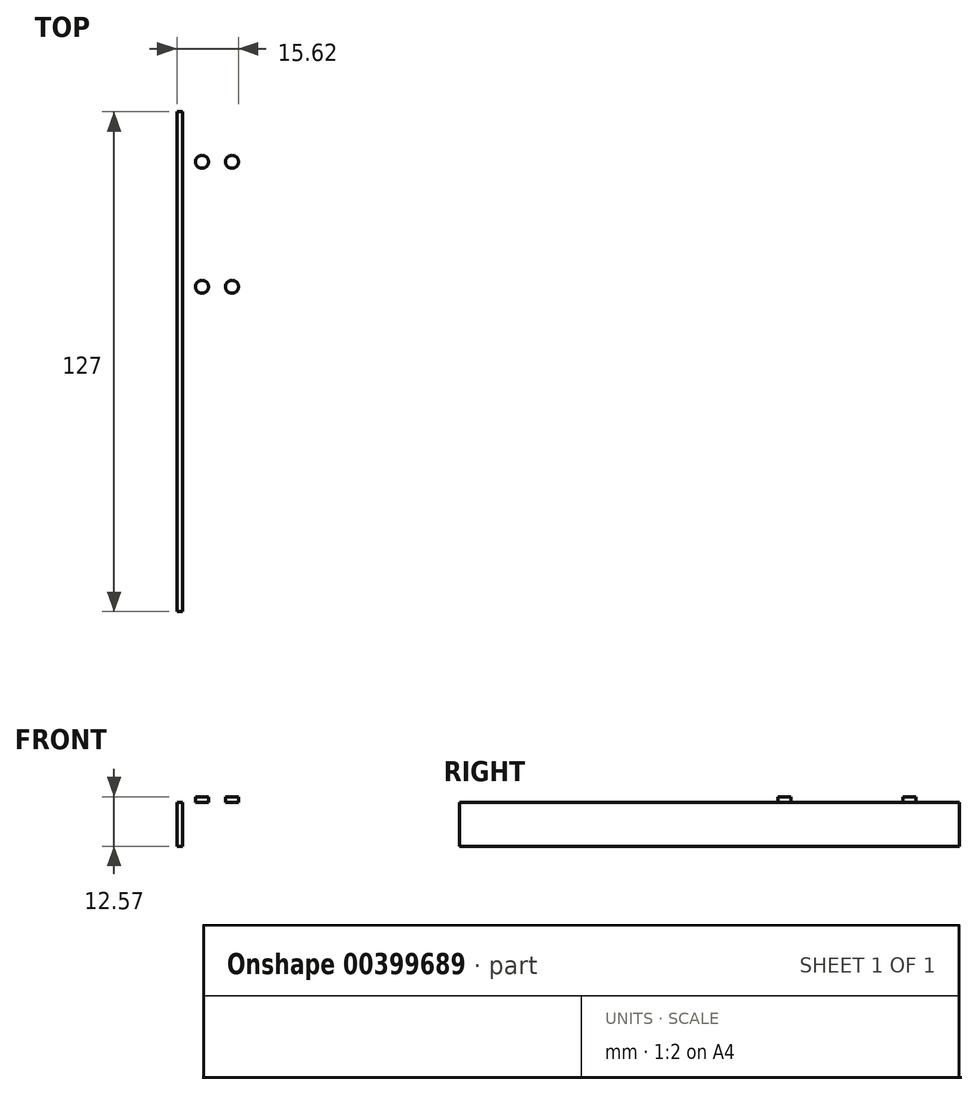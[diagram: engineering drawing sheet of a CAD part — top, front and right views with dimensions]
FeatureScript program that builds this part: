
annotation { "Feature Type Name" : "Feature", "Feature Type Description" : "" }
export const myFeature = defineFeature(function(context is Context, id is Id, definition is map)
    precondition{}
    {
        {
            var Q0;
            Q0=qCreatedBy(makeId("Front.planeOp"),FACE);
            var sketch = newSketch(context, id + "F0", { "sketchPlane" : qUnion([Q0])});
            skLineSegment(sketch, "E0.bottom", {"start": v(0, -11.1) * mm, "end": v(-1.47, -11.1) * mm});
            skLineSegment(sketch, "E0.top", {"start": v(0, 1.47) * mm, "end": v(-1.47, 1.47) * mm});
            skLineSegment(sketch, "E0.left", {"start": v(0, -11.1) * mm, "end": v(0, 1.47) * mm});
            skLineSegment(sketch, "E0.right", {"start": v(-1.47, -11.1) * mm, "end": v(-1.47, 1.47) * mm});
            skLineSegment(sketch, "E1.bottom", {"start": v(-1.47, 1.47) * mm, "end": v(17.58, 1.47) * mm});
            skLineSegment(sketch, "E1.top", {"start": v(-1.47, 0) * mm, "end": v(17.58, 0) * mm});
            skLineSegment(sketch, "E1.left", {"start": v(-1.47, 1.47) * mm, "end": v(-1.47, 0) * mm});
            skLineSegment(sketch, "E1.right", {"start": v(17.58, 1.47) * mm, "end": v(17.58, 0) * mm});
            skSolve(sketch);
        }
        {
            var Q0;
            {var subQ0=sQuery(id+"F0.wireOp",EDGE,"E0.bottom");Q0=makeQuery(id+"F0.imprint","IMPRINT",FACE,{"disambiguationData":[TD([[makeQuery(id+"F0.imprint","IMPRINT",EDGE,{"derivedFrom":subQ0}),-1.0]])]});}
            var Q1;
            {var subQ5=sQuery(id+"F0.wireOp",EDGE,"E1.left");Q1=makeQuery(id+"F0.imprint","IMPRINT",FACE,{"disambiguationData":[TD([[makeQuery(id+"F0.imprint","IMPRINT",EDGE,{"derivedFrom":subQ5}),1.0]])]});}
            var Q2;
            {var subQ5=sQuery(id+"F0.wireOp",EDGE,"E1.right");Q2=makeQuery(id+"F0.imprint","IMPRINT",FACE,{"disambiguationData":[TD([[makeQuery(id+"F0.imprint","IMPRINT",EDGE,{"derivedFrom":subQ5}),-1.0]])]});}
            extrude(context, id + "F1", {"entities" : qUnion([Q0, Q1, Q2]), "endBound" : BoundingType.SYMMETRIC, "depth" : 127 * mm});
        }
        {
            var Q0;
            Q0=makeQuery(id+"F1.opExtrude","SWEPT_FACE",FACE,{"disambiguationData":[OSD([sQuery(id+"F0.wireOp",EDGE,"E1.bottom")])]});
            var sketch = newSketch(context, id + "F2", { "sketchPlane" : qUnion([Q0])});
            skLineSegment(sketch, "E2", {"start": v(-1.47, 0) * mm, "end": v(17.58, 0) * mm, "construction": true});
            skLineSegment(sketch, "E3.0", {"start": v(17.58, -63.5) * mm, "end": v(17.58, 63.5) * mm, "construction": true});
            skLineSegment(sketch, "E4.0", {"start": v(-1.47, -63.5) * mm, "end": v(17.58, -63.5) * mm, "construction": true});
            skLineSegment(sketch, "E5", {"start": v(-1.47, -50.8) * mm, "end": v(17.58, -50.8) * mm, "construction": true});
            skCircle(sketch, "E6", {"center": v(12.5, -50.8) * mm, "radius": 1.65 * mm});
            skCircle(sketch, "E7", {"center": v(4.88, -50.8) * mm, "radius": 1.65 * mm});
            skLineSegment(sketch, "E8", {"start": v(4.88, -49.15) * mm, "end": v(12.5, -49.15) * mm});
            skLineSegment(sketch, "E9", {"start": v(12.5, -52.45) * mm, "end": v(4.88, -52.45) * mm});
            skLineSegment(sketch, "E10.0.1.0", {"start": v(4.88, -17.4) * mm, "end": v(12.5, -17.4) * mm});
            skCircle(sketch, "E10.0.1.1", {"center": v(4.88, -19.05) * mm, "radius": 1.65 * mm});
            skLineSegment(sketch, "E10.0.1.2", {"start": v(12.5, -20.7) * mm, "end": v(4.88, -20.7) * mm});
            skCircle(sketch, "E10.0.1.3", {"center": v(12.5, -19.05) * mm, "radius": 1.65 * mm});
            skLineSegment(sketch, "E10.direction2", {"start": v(4.88, -49.15) * mm, "end": v(4.88, -17.4) * mm, "construction": true});
            skLineSegment(sketch, "E11.MirrorCS", {"start": v(4.88, 17.4) * mm, "end": v(12.5, 17.4) * mm});
            skLineSegment(sketch, "E12.MirrorCS", {"start": v(12.5, 20.7) * mm, "end": v(4.88, 20.7) * mm});
            skCircle(sketch, "E13.MirrorC", {"center": v(4.88, 19.05) * mm, "radius": 1.65 * mm});
            skCircle(sketch, "E14.MirrorC", {"center": v(12.5, 19.05) * mm, "radius": 1.65 * mm});
            skCircle(sketch, "E15.MirrorC", {"center": v(12.5, 50.8) * mm, "radius": 1.65 * mm});
            skLineSegment(sketch, "E16.MirrorCS", {"start": v(12.5, 52.45) * mm, "end": v(4.88, 52.45) * mm});
            skCircle(sketch, "E17.MirrorC", {"center": v(4.88, 50.8) * mm, "radius": 1.65 * mm});
            skLineSegment(sketch, "E18.MirrorCS", {"start": v(4.88, 49.15) * mm, "end": v(12.5, 49.15) * mm});
            skSolve(sketch);
        }
        {
            var Q0;
            {var subQ0=sQuery(id+"F2.wireOp",EDGE,"E8");Q0=makeQuery(id+"F2.imprint","IMPRINT",FACE,{"disambiguationData":[TD([[makeQuery(id+"F2.imprint","IMPRINT",EDGE,{"derivedFrom":subQ0}),-1.0]])]});}
            var Q1;
            {var subQ0=sQuery(id+"F2.wireOp",EDGE,"E7");var subQ1=makeQuery(id+"F2.imprint","INTERSECT",VERTEX,{"derivedFrom":[subQ0,sQuery(id+"F2.wireOp",EDGE,"E8")]});Q1=makeQuery(id+"F2.imprint","IMPRINT",FACE,{"disambiguationData":[TD([[makeQuery(id+"F2.imprint","IMPRINT",EDGE,{"disambiguationData":[TD([[subQ1,-1.0]])],"derivedFrom":subQ0}),1.0]])]});}
            var Q2;
            {var subQ0=sQuery(id+"F2.wireOp",EDGE,"E6");var subQ1=makeQuery(id+"F2.imprint","INTERSECT",VERTEX,{"derivedFrom":[subQ0,sQuery(id+"F2.wireOp",EDGE,"E8")]});Q2=makeQuery(id+"F2.imprint","IMPRINT",FACE,{"disambiguationData":[TD([[makeQuery(id+"F2.imprint","IMPRINT",EDGE,{"disambiguationData":[TD([[subQ1,-1.0]])],"derivedFrom":subQ0}),1.0]])]});}
            var Q3;
            {var subQ0=sQuery(id+"F2.wireOp",EDGE,"E10.0.1.3");var subQ1=makeQuery(id+"F2.imprint","INTERSECT",VERTEX,{"derivedFrom":[sQuery(id+"F2.wireOp",EDGE,"E10.0.1.0"),subQ0]});Q3=makeQuery(id+"F2.imprint","IMPRINT",FACE,{"disambiguationData":[TD([[makeQuery(id+"F2.imprint","IMPRINT",EDGE,{"disambiguationData":[TD([[subQ1,-1.0]])],"derivedFrom":subQ0}),1.0]])]});}
            var Q4;
            {var subQ0=sQuery(id+"F2.wireOp",EDGE,"E10.0.1.0");Q4=makeQuery(id+"F2.imprint","IMPRINT",FACE,{"disambiguationData":[TD([[makeQuery(id+"F2.imprint","IMPRINT",EDGE,{"derivedFrom":subQ0}),-1.0]])]});}
            var Q5;
            {var subQ0=sQuery(id+"F2.wireOp",EDGE,"E10.0.1.1");var subQ1=makeQuery(id+"F2.imprint","INTERSECT",VERTEX,{"derivedFrom":[sQuery(id+"F2.wireOp",EDGE,"E10.0.1.0"),subQ0]});Q5=makeQuery(id+"F2.imprint","IMPRINT",FACE,{"disambiguationData":[TD([[makeQuery(id+"F2.imprint","IMPRINT",EDGE,{"disambiguationData":[TD([[subQ1,-1.0]])],"derivedFrom":subQ0}),1.0]])]});}
            var Q6;
            {var subQ0=sQuery(id+"F2.wireOp",EDGE,"E14.MirrorC");var subQ1=makeQuery(id+"F2.imprint","INTERSECT",VERTEX,{"derivedFrom":[sQuery(id+"F2.wireOp",EDGE,"E11.MirrorCS"),subQ0]});Q6=makeQuery(id+"F2.imprint","IMPRINT",FACE,{"disambiguationData":[TD([[makeQuery(id+"F2.imprint","IMPRINT",EDGE,{"disambiguationData":[TD([[subQ1,-1.0]])],"derivedFrom":subQ0}),-1.0]])]});}
            var Q7;
            {var subQ0=sQuery(id+"F2.wireOp",EDGE,"E11.MirrorCS");Q7=makeQuery(id+"F2.imprint","IMPRINT",FACE,{"disambiguationData":[TD([[makeQuery(id+"F2.imprint","IMPRINT",EDGE,{"derivedFrom":subQ0}),1.0]])]});}
            var Q8;
            {var subQ0=sQuery(id+"F2.wireOp",EDGE,"E13.MirrorC");var subQ1=makeQuery(id+"F2.imprint","INTERSECT",VERTEX,{"derivedFrom":[sQuery(id+"F2.wireOp",EDGE,"E11.MirrorCS"),subQ0]});Q8=makeQuery(id+"F2.imprint","IMPRINT",FACE,{"disambiguationData":[TD([[makeQuery(id+"F2.imprint","IMPRINT",EDGE,{"disambiguationData":[TD([[subQ1,-1.0]])],"derivedFrom":subQ0}),-1.0]])]});}
            var Q9;
            {var subQ0=sQuery(id+"F2.wireOp",EDGE,"E15.MirrorC");var subQ1=makeQuery(id+"F2.imprint","INTERSECT",VERTEX,{"derivedFrom":[subQ0,sQuery(id+"F2.wireOp",EDGE,"E16.MirrorCS")]});Q9=makeQuery(id+"F2.imprint","IMPRINT",FACE,{"disambiguationData":[TD([[makeQuery(id+"F2.imprint","IMPRINT",EDGE,{"disambiguationData":[TD([[subQ1,1.0]])],"derivedFrom":subQ0}),-1.0]])]});}
            var Q10;
            {var subQ0=sQuery(id+"F2.wireOp",EDGE,"E16.MirrorCS");Q10=makeQuery(id+"F2.imprint","IMPRINT",FACE,{"disambiguationData":[TD([[makeQuery(id+"F2.imprint","IMPRINT",EDGE,{"derivedFrom":subQ0}),1.0]])]});}
            var Q11;
            {var subQ0=sQuery(id+"F2.wireOp",EDGE,"E17.MirrorC");var subQ1=makeQuery(id+"F2.imprint","INTERSECT",VERTEX,{"derivedFrom":[sQuery(id+"F2.wireOp",EDGE,"E16.MirrorCS"),subQ0]});Q11=makeQuery(id+"F2.imprint","IMPRINT",FACE,{"disambiguationData":[TD([[makeQuery(id+"F2.imprint","IMPRINT",EDGE,{"disambiguationData":[TD([[subQ1,1.0]])],"derivedFrom":subQ0}),-1.0]])]});}
            extrude(context, id + "F3", {"entities" : qUnion([Q0, Q1, Q2, Q3, Q4, Q5, Q6, Q7, Q8, Q9, Q10, Q11]), "operationType" : NewBodyOperationType.REMOVE, "endBound" : BoundingType.THROUGH_ALL, "oppositeDirection" : true, "depth" : 25.4 * mm});
        }
    });
